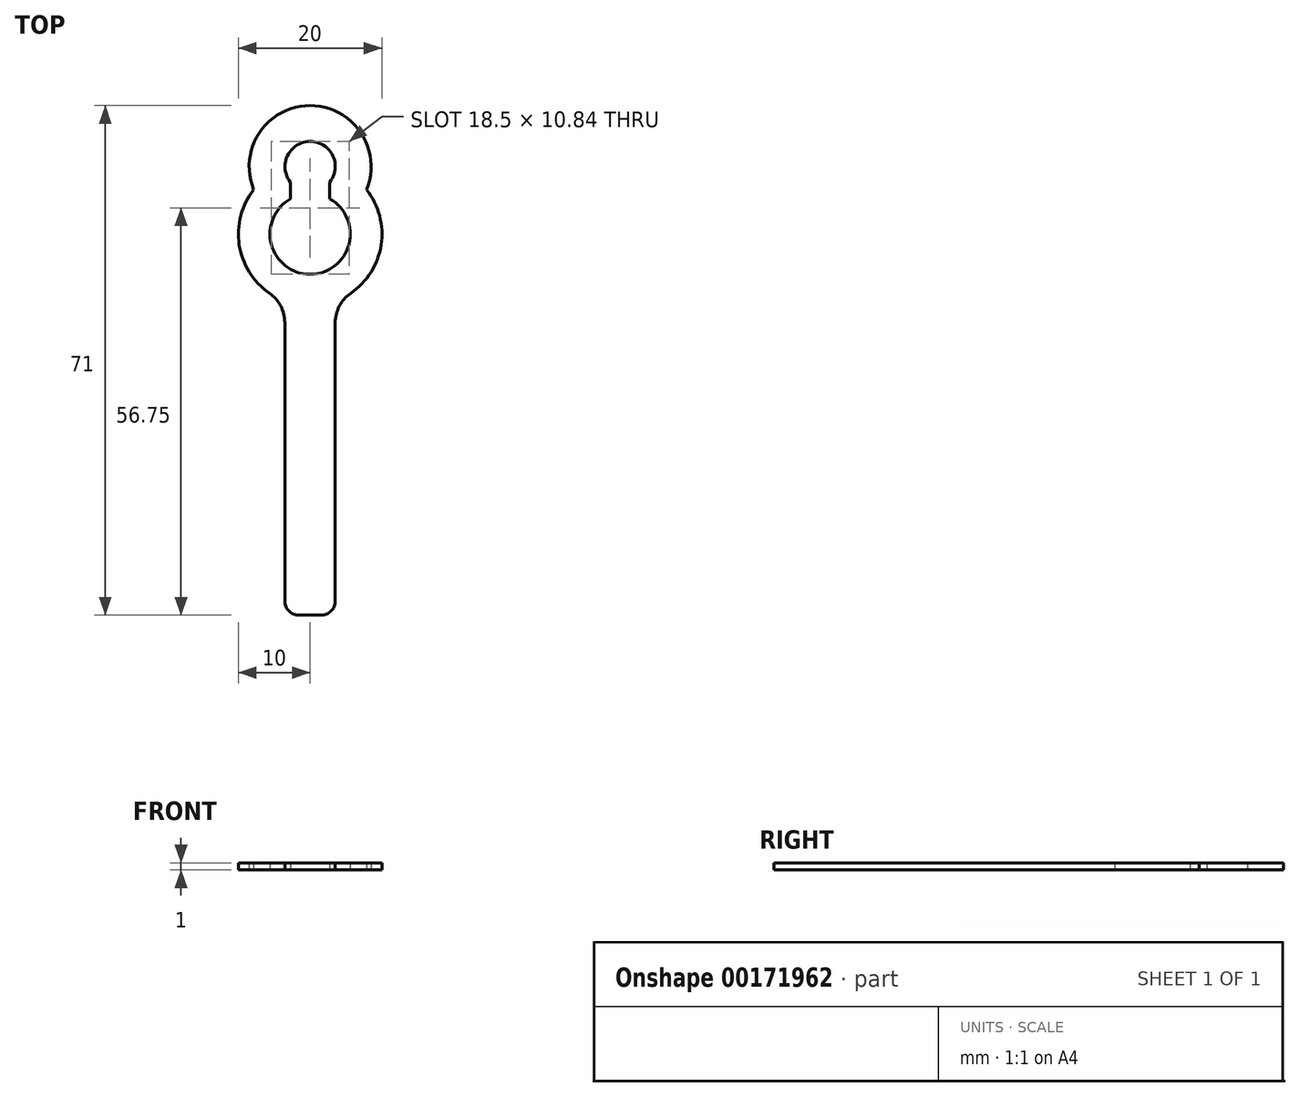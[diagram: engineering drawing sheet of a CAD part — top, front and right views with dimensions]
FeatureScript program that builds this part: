
annotation { "Feature Type Name" : "Feature", "Feature Type Description" : "" }
export const myFeature = defineFeature(function(context is Context, id is Id, definition is map)
    precondition{}
    {
        {
            var Q0;
            Q0=qCreatedBy(makeId("Top.planeOp"),FACE);
            var sketch = newSketch(context, id + "F0", { "sketchPlane" : qUnion([Q0])});
            skArc(sketch, "E0", {"start": v(-24.46, 44.17) * mm, "mid": v(-27.2, 49.86) * mm, "end": v(-29.92, 44.17) * mm});
            skArc(sketch, "E1", {"start": v(-29.92, 41.85) * mm, "mid": v(-27.2, 31.36) * mm, "end": v(-24.46, 41.85) * mm});
            skArc(sketch, "E2", {"start": v(-19.33, 43.13) * mm, "mid": v(-27.2, 54.86) * mm, "end": v(-35.06, 43.13) * mm});
            skArc(sketch, "E3", {"start": v(-35.06, 43.13) * mm, "mid": v(-37.08, 35.46) * mm, "end": v(-32.88, 28.73) * mm});
            skLineSegment(sketch, "E4", {"start": v(-29.92, 44.17) * mm, "end": v(-29.92, 41.85) * mm});
            skLineSegment(sketch, "E5", {"start": v(-24.46, 44.17) * mm, "end": v(-24.46, 41.85) * mm});
            skLineSegment(sketch, "E6.bottom", {"start": v(-30.7, 46.32) * mm, "end": v(-30.73, 46.32) * mm});
            skLineSegment(sketch, "E6.top", {"start": v(-25.7, -16.14) * mm, "end": v(-28.73, -16.14) * mm});
            skLineSegment(sketch, "E6.left", {"start": v(-23.7, 24.6) * mm, "end": v(-23.7, -14.14) * mm});
            skLineSegment(sketch, "E6.right", {"start": v(-30.73, 46.32) * mm, "end": v(-30.73, 46.31) * mm});
            skArc(sketch, "E7.trimOffspring", {"start": v(-30.7, 46.32) * mm, "mid": v(-30.71, 46.32) * mm, "end": v(-30.73, 46.31) * mm});
            skLineSegment(sketch, "E8.trimOffspring", {"start": v(-30.73, 24.62) * mm, "end": v(-30.73, -14.14) * mm});
            skArc(sketch, "E9.trimOffspring", {"start": v(-21.53, 28.72) * mm, "mid": v(-17.3, 35.45) * mm, "end": v(-19.33, 43.13) * mm});
            skPoint(sketch, "E10.visualSharp", {"position": v(-30.73, 27.6) * mm});
            skArc(sketch, "E10.filletArc", {"start": v(-30.73, 24.62) * mm, "mid": v(-31.3, 26.94) * mm, "end": v(-32.88, 28.73) * mm});
            skPoint(sketch, "E11.visualSharp", {"position": v(-23.7, 27.59) * mm});
            skArc(sketch, "E11.filletArc", {"start": v(-21.53, 28.72) * mm, "mid": v(-23.12, 26.92) * mm, "end": v(-23.7, 24.6) * mm});
            skPoint(sketch, "E12.visualSharp", {"position": v(-30.73, -16.14) * mm});
            skArc(sketch, "E12.filletArc", {"start": v(-30.73, -14.14) * mm, "mid": v(-30.14, -15.56) * mm, "end": v(-28.73, -16.14) * mm});
            skPoint(sketch, "E13.visualSharp", {"position": v(-23.7, -16.14) * mm});
            skArc(sketch, "E13.filletArc", {"start": v(-25.7, -16.14) * mm, "mid": v(-24.28, -15.56) * mm, "end": v(-23.7, -14.14) * mm});
            skSolve(sketch);
        }
        {
            var Q0;
            Q0=qCreatedBy(makeId("Top.planeOp"),FACE);
            var sketch = newSketch(context, id + "F1", { "sketchPlane" : qUnion([Q0])});
            skLineSegment(sketch, "E14", {"start": v(1.5, -35.5) * mm, "end": v(-1.53, -35.5) * mm});
            skArc(sketch, "E15", {"start": v(5.67, 9.36) * mm, "mid": v(4.07, 7.57) * mm, "end": v(3.5, 5.24) * mm});
            skArc(sketch, "E16", {"start": v(7.86, 23.78) * mm, "mid": v(0, 35.5) * mm, "end": v(-7.86, 23.78) * mm});
            skArc(sketch, "E17", {"start": v(-3.53, -33.5) * mm, "mid": v(-2.95, -34.91) * mm, "end": v(-1.53, -35.5) * mm});
            skArc(sketch, "E18", {"start": v(-7.86, 23.78) * mm, "mid": v(-9.89, 16.1) * mm, "end": v(-5.69, 9.38) * mm});
            skLineSegment(sketch, "E19", {"start": v(-2.73, 24.8) * mm, "end": v(-2.73, 22.49) * mm});
            skLineSegment(sketch, "E20", {"start": v(3.5, 5.24) * mm, "end": v(3.5, -33.5) * mm});
            skLineSegment(sketch, "E21", {"start": v(-3.53, 5.26) * mm, "end": v(-3.53, -33.5) * mm});
            skArc(sketch, "E22", {"start": v(5.67, 9.36) * mm, "mid": v(9.89, 16.1) * mm, "end": v(7.86, 23.78) * mm});
            skArc(sketch, "E23", {"start": v(1.5, -35.5) * mm, "mid": v(2.91, -34.91) * mm, "end": v(3.5, -33.5) * mm});
            skLineSegment(sketch, "E24", {"start": v(2.73, 24.8) * mm, "end": v(2.73, 22.49) * mm});
            skArc(sketch, "E25", {"start": v(-3.53, 5.26) * mm, "mid": v(-4.1, 7.59) * mm, "end": v(-5.69, 9.38) * mm});
            skArc(sketch, "E26", {"start": v(2.73, 24.8) * mm, "mid": v(0, 30.5) * mm, "end": v(-2.73, 24.8) * mm});
            skArc(sketch, "E27", {"start": v(-2.73, 22.49) * mm, "mid": v(0, 12) * mm, "end": v(2.73, 22.49) * mm});
            skSolve(sketch);
        }
        {
            var Q0;
            Q0=makeQuery(id+"F1.imprint","IMPRINT",FACE,{"disambiguationData":[TD([[makeQuery(id+"F1.imprint","IMPRINT",EDGE,{"derivedFrom":sQuery(id+"F1.wireOp",EDGE,"E14")}),-1.0]])]});
            extrude(context, id + "F2", {"entities" : qUnion([Q0]), "depth" : 1 * mm});
        }
    });
